# Revit family: izveshatel_io_102-26_ex_isp_10
name_source: partatom
category: Датчики
revit_build: Autodesk Revit 2016 (Build: 20150714_1515(x64)
units: mm (PartAtom-declared; Revit-internal decimal feet)

## family parameters
Всегда вертикально = Да
На основе рабочей плоскости = Нет
Общий = Нет
При загрузке вырезать с полостями = Нет
Размер круглого соединителя = Использовать диаметр
Сохранять ориентацию аннотаций = Нет
Тип детали = Нормальный
Точка расчета площади = Нет

## types (1)
- ИО 102-26-Ех исп.10
    ADSK_Версия Revit = 2016
    ADSK_Единица измерения = шт.
    ADSK_Завод-изготовитель = ООО НПП "Магнито-Контакт"
    ADSK_Масса = 0.25
    ADSK_Материал = Пластик белый
    ADSK_Наименование = Извещатель охранный точечный магнитоконтактный взрывозащищенный ИО102-26 ПАШК.425119.008
    ADSK_Обозначение = исп.10
    ADSK_Размер_Высота = 20 мм
    ADSK_Размер_Длина = 130 мм
    ADSK_Размер_Ширина = 30 мм
    BL_BIM library = https://bimlib.ru
    URL = www.m-kontakt.ru/produkt/datch_dlya_magn_konstr/ayaks_v_vse.html
    Высота магнита = 20 мм
    Длина магнита = 130 мм
    Изготовитель = ООО НПП "Магнито-Контакт"
    Ключевая пометка = ﻿﻿                           ﻿       ﻿     ﻿       ​         ​       ​   ​                  ﻿      ​ ​  ​       ​     ​ ﻿​                    ﻿     ﻿       ﻿       ﻿     ​         ﻿               ﻿﻿
    Код по классификатору = ﻿﻿                           ﻿       ﻿     ﻿       ​         ​       ​   ​                  ﻿      ​ ​  ​       ​     ​ ﻿​                    ﻿     ﻿       ﻿       ﻿     ​         ﻿               ﻿﻿
    Комментарии к типоразмеру = ﻿﻿                           ﻿       ﻿     ﻿       ​         ​       ​   ​                  ﻿      ​ ​  ​       ​     ​ ﻿​                    ﻿     ﻿       ﻿       ﻿     ​         ﻿               ﻿﻿
    Метизы = Нет
    Описание = ﻿﻿                           ﻿       ﻿     ﻿       ​         ​       ​   ​                  ﻿      ​ ​  ​       ​     ​ ﻿​                    ﻿     ﻿       ﻿       ﻿     ​         ﻿               ﻿﻿
    Ширина магнита = 30 мм
    исп.00 = Да
    исп.200/250 = Нет

## geometry (parser evidence)
native form markers: Blend x2
no freeform markers — native parametric forms only
